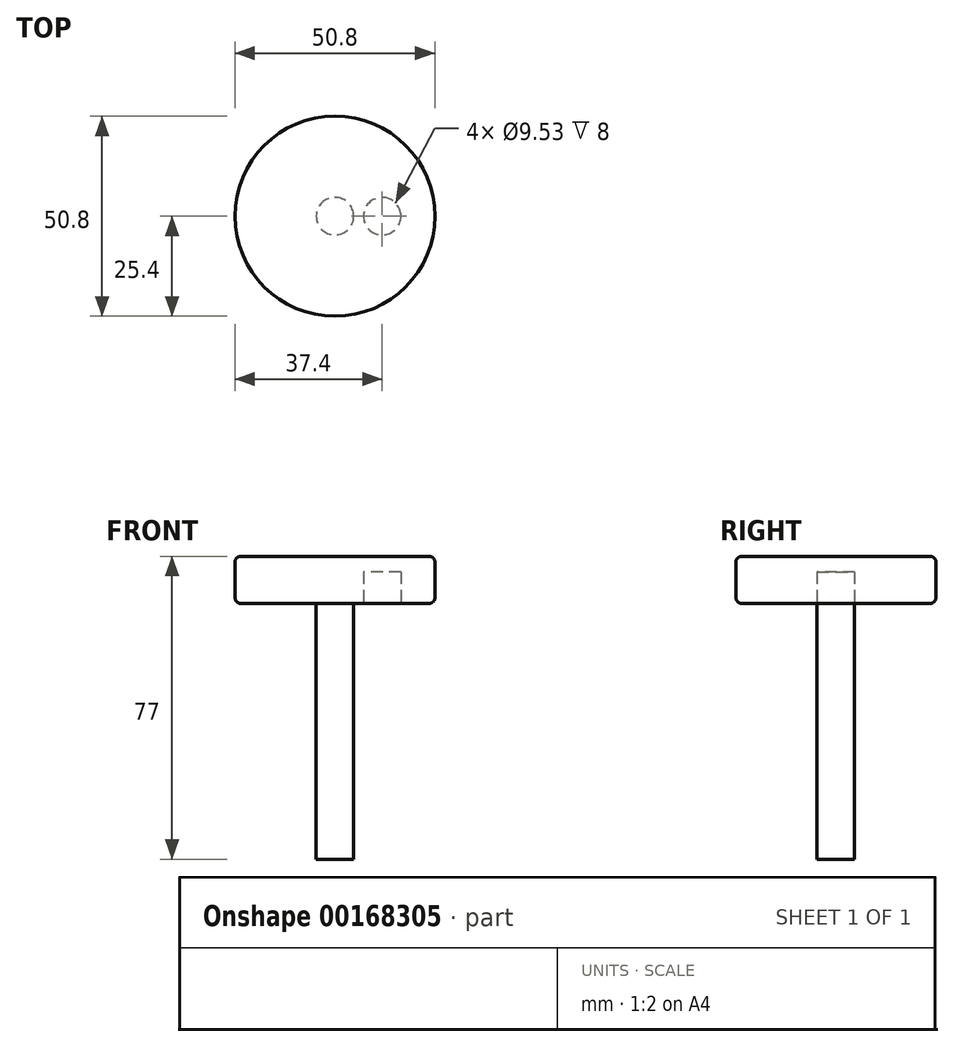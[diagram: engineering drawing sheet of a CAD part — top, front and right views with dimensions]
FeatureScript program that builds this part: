
annotation { "Feature Type Name" : "Feature", "Feature Type Description" : "" }
export const myFeature = defineFeature(function(context is Context, id is Id, definition is map)
    precondition{}
    {
        {
            var Q0;
            Q0=qCreatedBy(makeId("Top.planeOp"),FACE);
            var sketch = newSketch(context, id + "F0", { "sketchPlane" : qUnion([Q0])});
            skCircle(sketch, "E0", {"center": v(0, 0) * mm, "radius": 25.4 * mm});
            skSolve(sketch);
        }
        {
            var Q0;
            Q0=makeQuery(id+"F0.imprint","IMPRINT",FACE,{"disambiguationData":[TD([[makeQuery(id+"F0.imprint","IMPRINT",EDGE,{"derivedFrom":sQuery(id+"F0.wireOp",EDGE,"E0")}),1.0]])]});
            extrude(context, id + "F1", {"entities" : qUnion([Q0]), "depth" : 12 * mm});
        }
        {
            var Q0;
            Q0=makeQuery(id+"F1.opExtrude","CAP_EDGE",EDGE,{"disambiguationData":[OSD([sQuery(id+"F0.wireOp",EDGE,"E0")])],"isStart":false});
            var Q1;
            Q1=makeQuery(id+"F1.opExtrude","CAP_EDGE",EDGE,{"disambiguationData":[OSD([sQuery(id+"F0.wireOp",EDGE,"E0")])],"isStart":true});
            fillet(context, id + "F2", {"entities" : qUnion([Q0, Q1]), "radius" : 1.5 * mm, "tangentPropagation" : true, "allowEdgeOverflow" : false});
        }
        {
            var Q0;
            Q0=qCreatedBy(makeId("Top.planeOp"),FACE);
            var sketch = newSketch(context, id + "F3", { "sketchPlane" : qUnion([Q0])});
            skCircle(sketch, "E1", {"center": v(12, 0) * mm, "radius": 4.76 * mm});
            skSolve(sketch);
        }
        {
            var Q0;
            Q0=makeQuery(id+"F3.imprint","IMPRINT",FACE,{"disambiguationData":[TD([[makeQuery(id+"F3.imprint","IMPRINT",EDGE,{"derivedFrom":sQuery(id+"F3.wireOp",EDGE,"E1")}),1.0]])]});
            extrude(context, id + "F4", {"entities" : qUnion([Q0]), "operationType" : NewBodyOperationType.REMOVE, "depth" : 8 * mm});
        }
        {
            var Q0;
            Q0=qCreatedBy(makeId("Top.planeOp"),FACE);
            var sketch = newSketch(context, id + "F5", { "sketchPlane" : qUnion([Q0])});
            skCircle(sketch, "E2", {"center": v(0, 0) * mm, "radius": 4.76 * mm});
            skSolve(sketch);
        }
        {
            var Q0;
            Q0=makeQuery(id+"F5.imprint","IMPRINT",FACE,{"disambiguationData":[TD([[makeQuery(id+"F5.imprint","IMPRINT",EDGE,{"derivedFrom":sQuery(id+"F5.wireOp",EDGE,"E2")}),1.0]])]});
            extrude(context, id + "F6", {"entities" : qUnion([Q0]), "oppositeDirection" : true, "depth" : 65 * mm});
        }
    });
